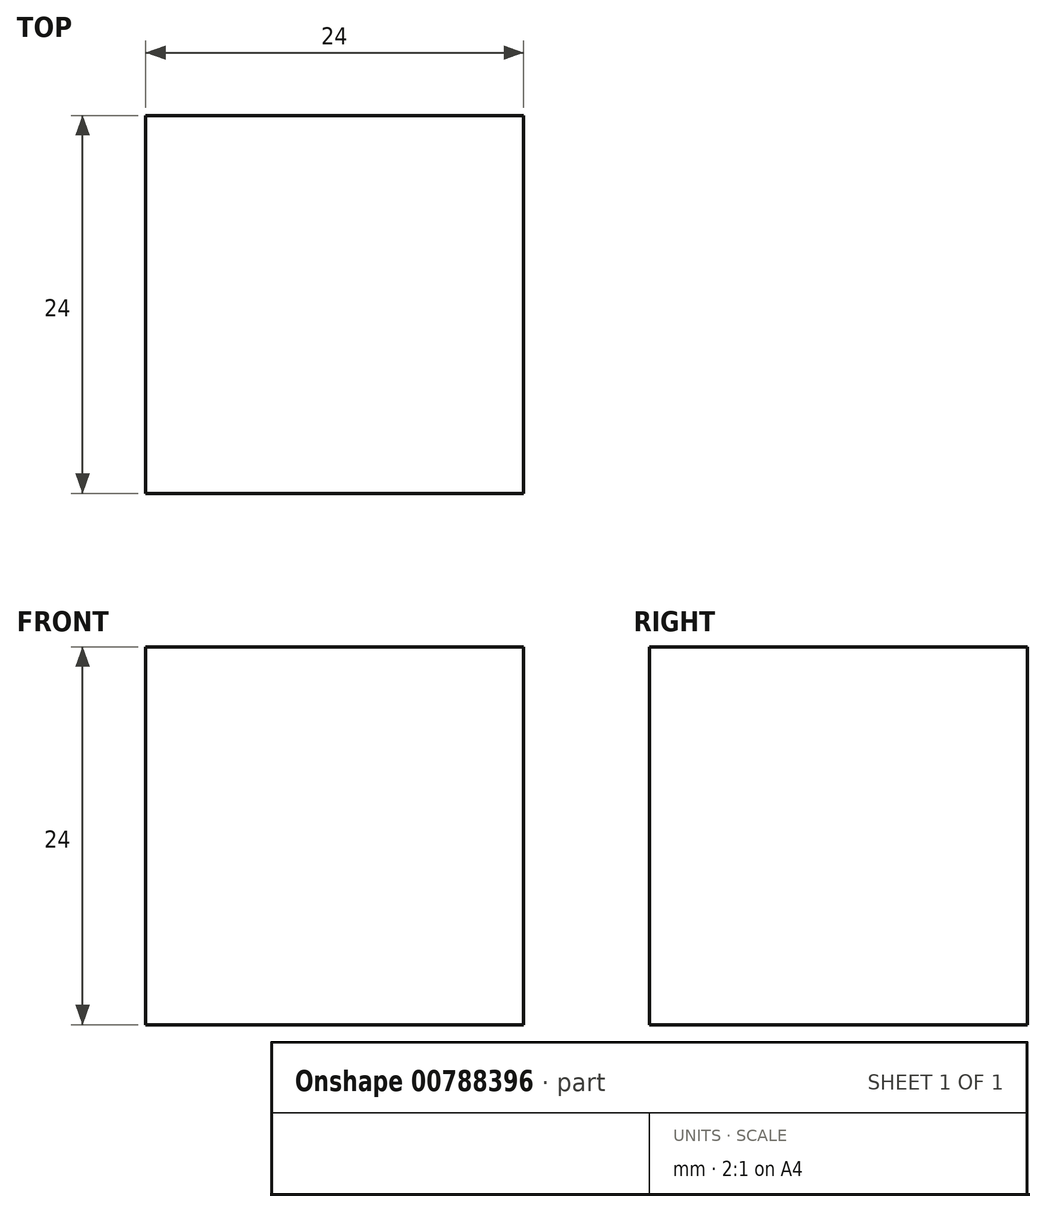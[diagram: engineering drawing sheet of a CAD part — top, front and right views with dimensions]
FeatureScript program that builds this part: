
annotation { "Feature Type Name" : "Feature", "Feature Type Description" : "" }
export const myFeature = defineFeature(function(context is Context, id is Id, definition is map)
    precondition{}
    {
        {
            var Q0;
            Q0=qCreatedBy(makeId("Top.planeOp"),FACE);
            var sketch = newSketch(context, id + "F0", { "sketchPlane" : qUnion([Q0])});
            skLineSegment(sketch, "E0.bottom", {"start": v(12, 12) * mm, "end": v(-12, 12) * mm});
            skLineSegment(sketch, "E0.top", {"start": v(12, -12) * mm, "end": v(-12, -12) * mm});
            skLineSegment(sketch, "E0.left", {"start": v(12, 12) * mm, "end": v(12, -12) * mm});
            skLineSegment(sketch, "E0.right", {"start": v(-12, 12) * mm, "end": v(-12, -12) * mm});
            skPoint(sketch, "E0.middle", {"position": v(0, 0) * mm});
            skSolve(sketch);
        }
        {
            var Q0;
            Q0=makeQuery(id+"F0.imprint","IMPRINT",FACE,{"disambiguationData":[TD([[makeQuery(id+"F0.imprint","IMPRINT",EDGE,{"derivedFrom":sQuery(id+"F0.wireOp",EDGE,"E0.bottom")}),1.0]])]});
            extrude(context, id + "F1", {"entities" : qUnion([Q0]), "depth" : 24 * mm, "offsetDistance" : 25 * mm});
        }
    });
